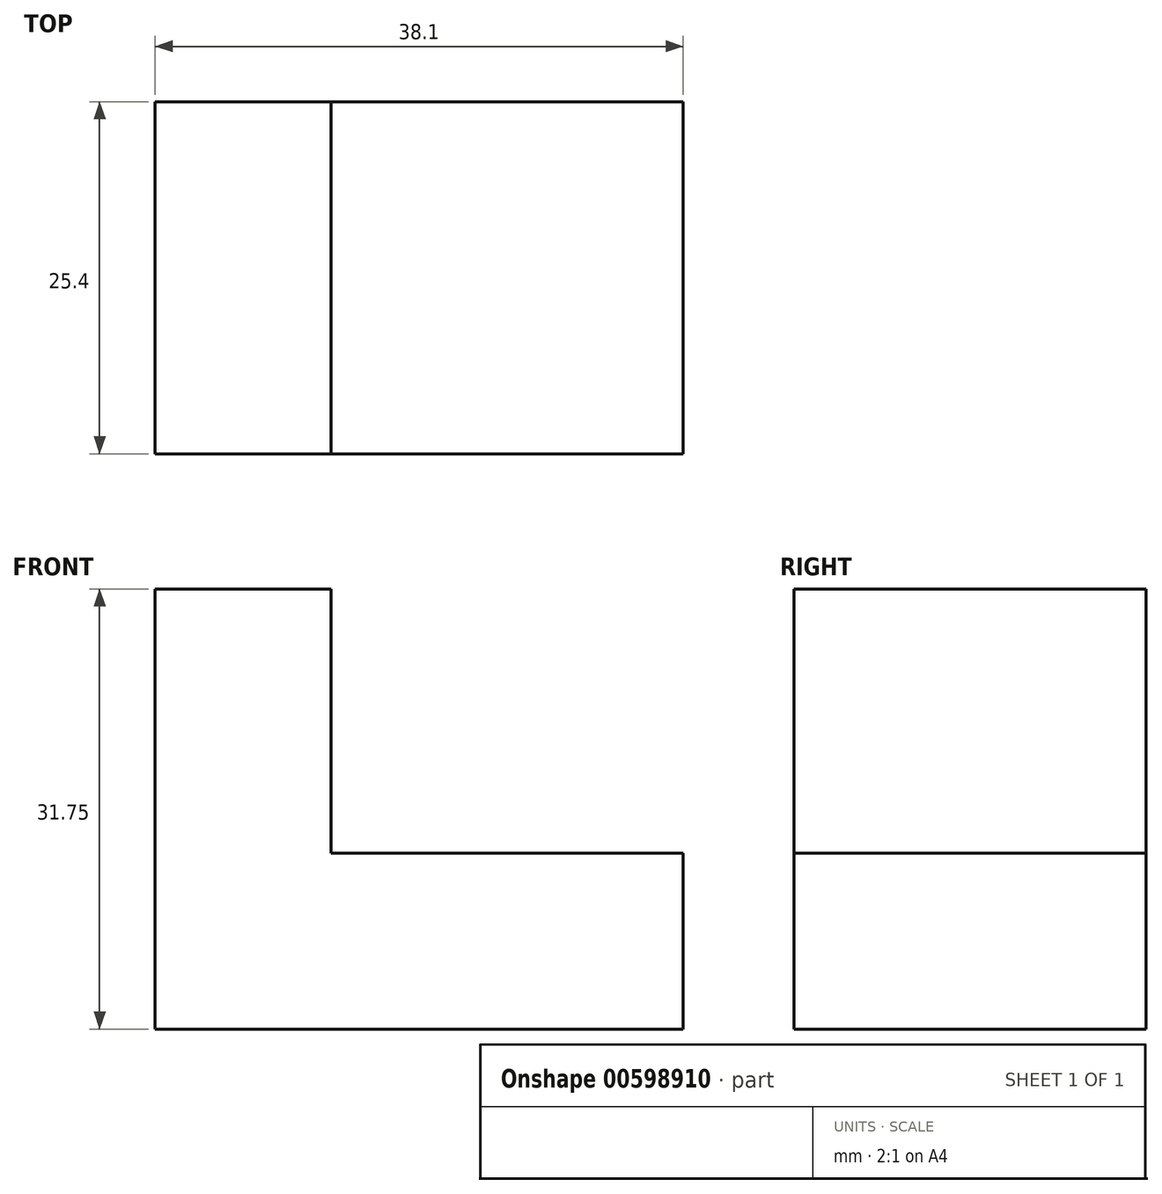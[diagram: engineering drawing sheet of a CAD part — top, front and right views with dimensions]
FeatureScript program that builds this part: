
annotation { "Feature Type Name" : "Feature", "Feature Type Description" : "" }
export const myFeature = defineFeature(function(context is Context, id is Id, definition is map)
    precondition{}
    {
        {
            var Q0;
            Q0=qCreatedBy(makeId("Front.planeOp"),FACE);
            var sketch = newSketch(context, id + "F0", { "sketchPlane" : qUnion([Q0])});
            skPoint(sketch, "E0.end.orphan", {"position": v(46.29, 0) * mm});
            skLineSegment(sketch, "E1", {"start": v(0, 0) * mm, "end": v(0, 31.75) * mm});
            skLineSegment(sketch, "E2", {"start": v(0, 31.75) * mm, "end": v(12.7, 31.75) * mm});
            skLineSegment(sketch, "E3", {"start": v(12.7, 31.75) * mm, "end": v(12.7, 12.7) * mm});
            skLineSegment(sketch, "E4", {"start": v(12.7, 12.7) * mm, "end": v(38.1, 12.7) * mm});
            skLineSegment(sketch, "E5", {"start": v(0, 0) * mm, "end": v(38.1, 0) * mm});
            skLineSegment(sketch, "E6", {"start": v(38.1, 12.7) * mm, "end": v(38.1, 0) * mm});
            skSolve(sketch);
        }
        {
            var Q0;
            Q0=makeQuery(id+"F0.imprint","IMPRINT",FACE,{"disambiguationData":[TD([[makeQuery(id+"F0.imprint","IMPRINT",EDGE,{"derivedFrom":sQuery(id+"F0.wireOp",EDGE,"E1")}),-1.0]])]});
            extrude(context, id + "F1", {"entities" : qUnion([Q0]), "depth" : 25.4 * mm, "offsetDistance" : 25.4 * mm});
        }
    });
